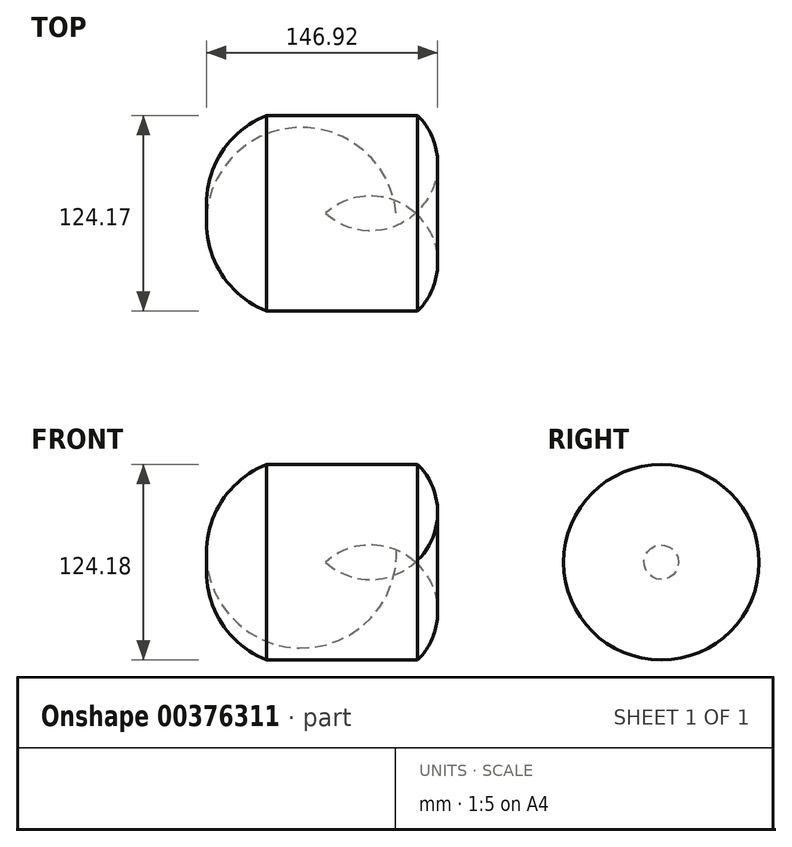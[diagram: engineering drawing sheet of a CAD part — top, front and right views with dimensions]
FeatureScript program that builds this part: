
annotation { "Feature Type Name" : "Feature", "Feature Type Description" : "" }
export const myFeature = defineFeature(function(context is Context, id is Id, definition is map)
    precondition{}
    {
        {
            var Q0;
            Q0=qCreatedBy(makeId("Top.planeOp"),FACE);
            var sketch = newSketch(context, id + "F0", { "sketchPlane" : qUnion([Q0])});
            skLineSegment(sketch, "E0", {"start": v(-58.63, -76.28) * mm, "end": v(37.31, -76.28) * mm});
            skArc(sketch, "E1", {"start": v(-96.6, -14.2) * mm, "mid": v(-88.01, -51.6) * mm, "end": v(-58.63, -76.28) * mm});
            skLineSegment(sketch, "E2", {"start": v(-96.6, -14.2) * mm, "end": v(35.92, -14.2) * mm});
            skArc(sketch, "E3", {"start": v(37.31, -76.28) * mm, "mid": v(50.02, -44.94) * mm, "end": v(35.92, -14.2) * mm});
            skSolve(sketch);
        }
        {
            var Q0;
            Q0=makeQuery(id+"F0.imprint","IMPRINT",FACE,{"disambiguationData":[TD([[makeQuery(id+"F0.imprint","IMPRINT",EDGE,{"derivedFrom":sQuery(id+"F0.wireOp",EDGE,"E0")}),1.0]])]});
            var Q1;
            Q1=sQuery(id+"F0.wireOp",EDGE,"E2");
            revolve(context, id + "F1", {"entities" : qUnion([Q0]), "axis" : qUnion([Q1]), "revolveType" : RevolveType.FULL});
        }
    });
